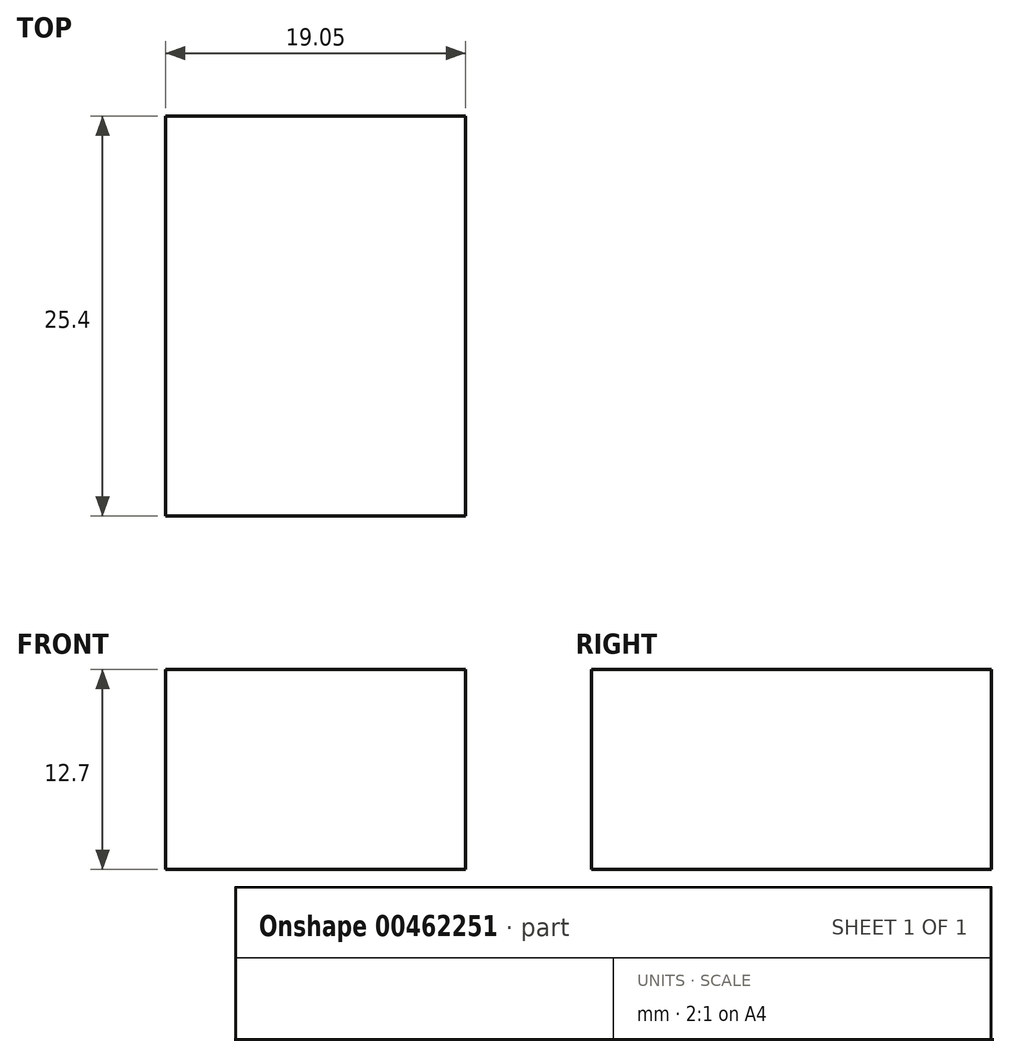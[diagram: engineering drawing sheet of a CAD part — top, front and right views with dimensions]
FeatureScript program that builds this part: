
annotation { "Feature Type Name" : "Feature", "Feature Type Description" : "" }
export const myFeature = defineFeature(function(context is Context, id is Id, definition is map)
    precondition{}
    {
        {
            var Q0;
            Q0=qCreatedBy(makeId("Front.planeOp"),FACE);
            var sketch = newSketch(context, id + "F0", { "sketchPlane" : qUnion([Q0])});
            skLineSegment(sketch, "E0.bottom", {"start": v(50.8, 25.4) * mm, "end": v(-50.8, 25.4) * mm});
            skLineSegment(sketch, "E0.top", {"start": v(50.8, -25.4) * mm, "end": v(-50.8, -25.4) * mm});
            skLineSegment(sketch, "E0.left", {"start": v(50.8, 25.4) * mm, "end": v(50.8, -25.4) * mm});
            skLineSegment(sketch, "E0.right", {"start": v(-50.8, 25.4) * mm, "end": v(-50.8, -25.4) * mm});
            skPoint(sketch, "E0.middle", {"position": v(0, 0) * mm});
            skLineSegment(sketch, "E1.bottom", {"start": v(-25.4, 25.4) * mm, "end": v(25.4, 25.4) * mm});
            skLineSegment(sketch, "E1.top", {"start": v(-25.4, 12.7) * mm, "end": v(25.4, 12.7) * mm});
            skLineSegment(sketch, "E1.left", {"start": v(-25.4, 25.4) * mm, "end": v(-25.4, 12.7) * mm});
            skLineSegment(sketch, "E1.right", {"start": v(25.4, 25.4) * mm, "end": v(25.4, 12.7) * mm});
            skLineSegment(sketch, "E2.bottom", {"start": v(50.8, -12.7) * mm, "end": v(31.75, -12.7) * mm});
            skLineSegment(sketch, "E2.top", {"start": v(50.8, -25.4) * mm, "end": v(31.75, -25.4) * mm});
            skLineSegment(sketch, "E2.left", {"start": v(50.8, -12.7) * mm, "end": v(50.8, -25.4) * mm});
            skLineSegment(sketch, "E2.right", {"start": v(31.75, -12.7) * mm, "end": v(31.75, -25.4) * mm});
            skSolve(sketch);
        }
        {
            var Q0;
            Q0=makeQuery(id+"F0.imprint","IMPRINT",FACE,{"disambiguationData":[TD([[makeQuery(id+"F0.imprint","IMPRINT",EDGE,{"derivedFrom":sQuery(id+"F0.wireOp",EDGE,"E0.top")}),-1.0]])]});
            extrude(context, id + "F1", {"entities" : qUnion([Q0]), "depth" : 25.4 * mm});
        }
        {
            var Q0;
            Q0=makeQuery(id+"F1.opExtrude","SWEPT_FACE",FACE,{"disambiguationData":[OSD([sQuery(id+"F0.wireOp",EDGE,"E0.left")])]});
            var sketch = newSketch(context, id + "F2", { "sketchPlane" : qUnion([Q0])});
            skCircle(sketch, "E3", {"center": v(-12.7, 0) * mm, "radius": 6.35 * mm});
            skSolve(sketch);
        }
        {
            var Q0;
            Q0=makeQuery(id+"F2.imprint","IMPRINT",FACE,{"disambiguationData":[TD([[makeQuery(id+"F2.imprint","IMPRINT",EDGE,{"derivedFrom":sQuery(id+"F2.wireOp",EDGE,"E3")}),1.0]])]});
            extrude(context, id + "F3", {"entities" : qUnion([Q0]), "operationType" : NewBodyOperationType.REMOVE, "endBound" : BoundingType.THROUGH_ALL, "oppositeDirection" : true, "depth" : 25.4 * mm});
        }
    });
